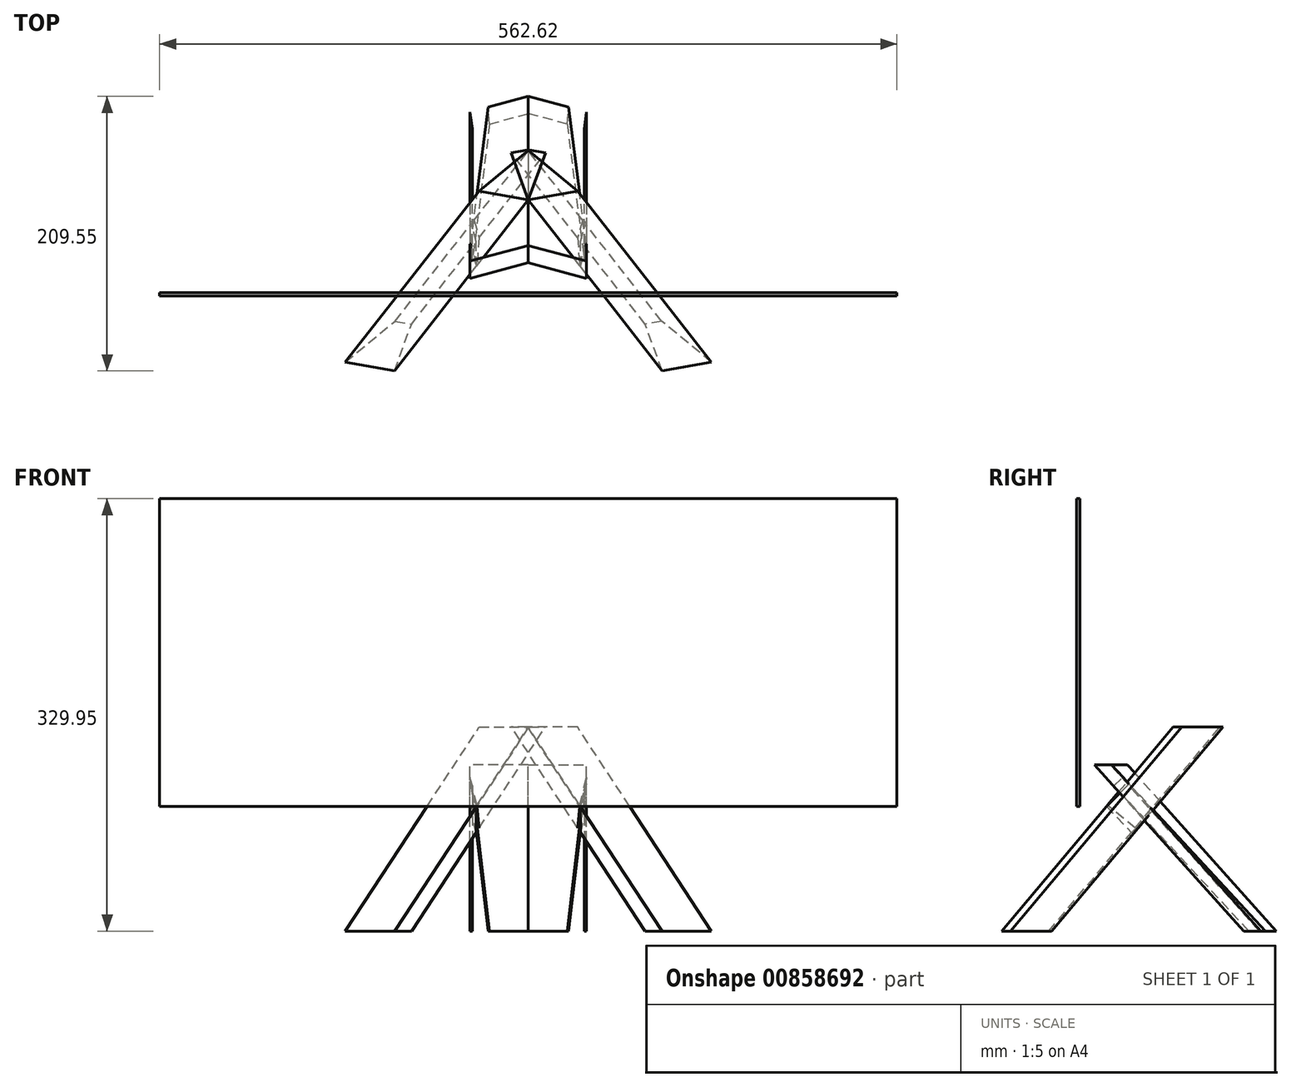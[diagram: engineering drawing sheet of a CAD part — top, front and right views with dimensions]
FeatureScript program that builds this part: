
annotation { "Feature Type Name" : "Feature", "Feature Type Description" : "" }
export const myFeature = defineFeature(function(context is Context, id is Id, definition is map)
    precondition{}
    {
        {
            var Q0;
            Q0=qCreatedBy(makeId("Right.planeOp"),FACE);
            cPlane(context, id + "F0", {"entities" : qUnion([Q0]), "cplaneType" : CPlaneType.OFFSET, "offset" : 139.7 * mm, "width" : 152.4 * mm, "height" : 152.4 * mm});
        }
        {
            var Q0;
            Q0=qCreatedBy(makeId("Front.planeOp"),FACE);
            cPlane(context, id + "F1", {"entities" : qUnion([Q0]), "cplaneType" : CPlaneType.OFFSET, "offset" : 82.55 * mm, "width" : 152.4 * mm, "height" : 152.4 * mm});
        }
        {
            var Q0;
            Q0=qCreatedBy(makeId("Front.planeOp"),FACE);
            cPlane(context, id + "F2", {"entities" : qUnion([Q0]), "cplaneType" : CPlaneType.OFFSET, "offset" : 127 * mm, "oppositeDirection" : true, "width" : 152.4 * mm, "height" : 152.4 * mm});
        }
        {
            var Q0;
            Q0=qCreatedBy(makeId("Front.planeOp"),FACE);
            cPlane(context, id + "F3", {"entities" : qUnion([Q0]), "cplaneType" : CPlaneType.OFFSET, "offset" : 25.4 * mm, "width" : 152.4 * mm, "height" : 152.4 * mm});
        }
        {
            var Q0;
            Q0=qCreatedBy(makeId("Top.planeOp"),FACE);
            var sketch = newSketch(context, id + "F4", { "sketchPlane" : qUnion([Q0])});
            skLineSegment(sketch, "E0", {"start": v(0, -82.55) * mm, "end": v(139.7, -82.55) * mm});
            skSolve(sketch);
        }
        {
            var Q0;
            Q0=qCreatedBy(id+"F3.planeOp",FACE);
            var sketch = newSketch(context, id + "F5", { "sketchPlane" : qUnion([Q0])});
            skLineSegment(sketch, "E1.bottom", {"start": v(-281.3, 95.25) * mm, "end": v(281.3, 95.25) * mm});
            skLineSegment(sketch, "E1.top", {"start": v(-281.3, 329.95) * mm, "end": v(281.3, 329.95) * mm});
            skLineSegment(sketch, "E1.left", {"start": v(-281.3, 95.25) * mm, "end": v(-281.3, 329.95) * mm});
            skLineSegment(sketch, "E1.right", {"start": v(281.3, 95.25) * mm, "end": v(281.3, 329.95) * mm});
            skLineSegment(sketch, "E2", {"start": v(-281.3, 329.95) * mm, "end": v(281.3, 95.25) * mm, "construction": true});
            skLineSegment(sketch, "E3", {"start": v(0, 0) * mm, "end": v(0, 212.6) * mm, "construction": true});
            skSolve(sketch);
        }
        {
            var Q0;
            Q0 = qSketchRegion(id + "F5", true);
            extrude(context, id + "F6", {"entities" : qUnion([Q0]), "oppositeDirection" : true, "depth" : 2.54 * mm, "offsetDistance" : 25.4 * mm});
        }
        {
            var Q0;
            Q0=qCreatedBy(makeId("Top.planeOp"),FACE);
            var sketch = newSketch(context, id + "F7", { "sketchPlane" : qUnion([Q0])});
            skLineSegment(sketch, "E4", {"start": v(139.7, -75.93) * mm, "end": v(102.18, -82.55) * mm});
            skLineSegment(sketch, "E5", {"start": v(102.18, -82.55) * mm, "end": v(89.15, -46.75) * mm});
            skLineSegment(sketch, "E6", {"start": v(139.7, -75.93) * mm, "end": v(101.65, -44.54) * mm});
            skLineSegment(sketch, "E7", {"start": v(101.65, -44.54) * mm, "end": v(89.15, -46.75) * mm});
            skSolve(sketch);
        }
        {
            var Q0;
            Q0=sQuery(id+"F4.wireOp",EDGE,"E0");
            cPlane(context, id + "F8", {"entities" : qUnion([Q0]), "cplaneType" : CPlaneType.LINE_ANGLE, "offset" : 25.4 * mm, "angle" : 40 * degree, "oppositeDirection" : true, "width" : 152.4 * mm, "height" : 152.4 * mm});
        }
        {
            var Q0;
            Q0=qCreatedBy(id+"F8.planeOp",FACE);
            var sketch = newSketch(context, id + "F9", { "sketchPlane" : qUnion([Q0])});
            skLineSegment(sketch, "E8", {"start": v(-102.18, -53.06) * mm, "end": v(0, 150.14) * mm});
            skSolve(sketch);
        }
        {
            var Q0;
            Q0=makeQuery(id+"F7.imprint","IMPRINT",FACE,{"disambiguationData":[TD([[makeQuery(id+"F7.imprint","IMPRINT",EDGE,{"derivedFrom":sQuery(id+"F7.wireOp",EDGE,"E4")}),-1.0]])]});
            var Q1;
            Q1=sQuery(id+"F9.wireOp",EDGE,"E8");
            sweep(context, id + "F10", {"profiles" : qUnion([Q0]), "path" : qUnion([Q1])});
        }
        {
            var Q0;
            Q0=qCreatedBy(makeId("Top.planeOp"),FACE);
            var sketch = newSketch(context, id + "F11", { "sketchPlane" : qUnion([Q0])});
            skLineSegment(sketch, "E9", {"start": v(0, 127) * mm, "end": v(44.45, 115.09) * mm});
            skLineSegment(sketch, "E10", {"start": v(44.45, 115.09) * mm, "end": v(44.45, 101.94) * mm});
            skLineSegment(sketch, "E11", {"start": v(44.45, 101.94) * mm, "end": v(0, 113.85) * mm});
            skLineSegment(sketch, "E12", {"start": v(0, 113.85) * mm, "end": v(0, 127) * mm});
            skSolve(sketch);
        }
        {
            var Q0;
            Q0=qCreatedBy(makeId("Right.planeOp"),FACE);
            var sketch = newSketch(context, id + "F12", { "sketchPlane" : qUnion([Q0])});
            skLineSegment(sketch, "E13", {"start": v(113.85, 0) * mm, "end": v(0, 127) * mm});
            skSolve(sketch);
        }
        {
            var Q0;
            Q0=makeQuery(id+"F11.imprint","IMPRINT",FACE,{"disambiguationData":[TD([[makeQuery(id+"F11.imprint","IMPRINT",EDGE,{"derivedFrom":sQuery(id+"F11.wireOp",EDGE,"E9")}),-1.0]])]});
            var Q1;
            Q1=sQuery(id+"F12.wireOp",EDGE,"E13");
            sweep(context, id + "F13", {"profiles" : qUnion([Q0]), "path" : qUnion([Q1])});
        }
        {
            var Q0;
            Q0=makeQuery(id+"F13.opSweep","SWEPT_FACE",FACE,{"disambiguationData":[OSD([sQuery(id+"F11.wireOp",EDGE,"E9"),sQuery(id+"F12.wireOp",EDGE,"E13")])]});
            var sketch = newSketch(context, id + "F14", { "sketchPlane" : qUnion([Q0])});
            skLineSegment(sketch, "E14", {"start": v(-28.74, 102.51) * mm, "end": v(-12.83, -79.28) * mm});
            skLineSegment(sketch, "E15", {"start": v(-26.82, -76.82) * mm, "end": v(-12.83, -79.28) * mm});
            skLineSegment(sketch, "E16", {"start": v(-38.68, 102.51) * mm, "end": v(-38.68, -74.74) * mm});
            skLineSegment(sketch, "E17", {"start": v(-28.74, 102.51) * mm, "end": v(-38.68, 102.51) * mm});
            skLineSegment(sketch, "E18", {"start": v(-38.68, -74.74) * mm, "end": v(-26.82, -76.82) * mm});
            skSolve(sketch);
        }
        {
            var Q0;
            {var subQ0=sQuery(id+"F14.wireOp",EDGE,"E15");Q0=makeQuery(id+"F14.imprint","IMPRINT",FACE,{"disambiguationData":[TD([[makeQuery(id+"F14.imprint","IMPRINT",EDGE,{"derivedFrom":subQ0}),1.0]])]});}
            var Q1;
            Q1=makeQuery(id+"F14.imprint","IMPRINT",FACE,{"disambiguationData":[TD([[makeQuery(id+"F14.imprint","IMPRINT",EDGE,{"derivedFrom":sQuery(id+"F14.wireOp",EDGE,"E16")}),-1.0]])]});
            extrude(context, id + "F15", {"entities" : qUnion([Q0, Q1]), "operationType" : NewBodyOperationType.REMOVE, "endBound" : BoundingType.THROUGH_ALL, "oppositeDirection" : true, "depth" : 25.4 * mm, "offsetDistance" : 25.4 * mm});
        }
        {
            var Q0;
            Q0=makeQuery(id+"F10.opSweep","SWEPT_BODY",BODY,{"disambiguationData":[OSD([sQuery(id+"F7.wireOp",EDGE,"E4"),sQuery(id+"F7.wireOp",EDGE,"E5"),sQuery(id+"F7.wireOp",EDGE,"nMThdsTY-C0K1-rSYk-cAk6-KEH7Uzmns5mL"),sQuery(id+"F9.wireOp",EDGE,"E8")])]});
            var Q1;
            Q1=makeQuery(id+"F13.opSweep","SWEPT_BODY",BODY,{"disambiguationData":[OSD([sQuery(id+"F11.wireOp",EDGE,"E9"),sQuery(id+"F11.wireOp",EDGE,"E10"),sQuery(id+"F11.wireOp",EDGE,"E11"),sQuery(id+"F11.wireOp",EDGE,"E12"),sQuery(id+"F12.wireOp",EDGE,"E13")])]});
            var Q2;
            Q2=qCreatedBy(makeId("Right.planeOp"),FACE);
            mirror(context, id + "F16", {"operationType" : NewBodyOperationType.ADD, "entities" : qUnion([Q0, Q1]), "mirrorPlane" : qUnion([Q2])});
        }
    });
